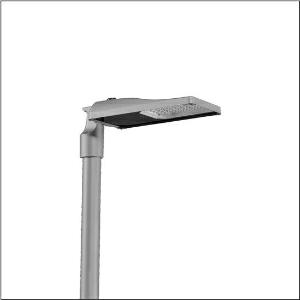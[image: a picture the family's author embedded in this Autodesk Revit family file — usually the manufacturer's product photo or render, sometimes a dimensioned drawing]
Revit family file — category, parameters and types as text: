
# Revit family: streetlight_sl_31_mini___st1_0a_5xh2d3as08ga_13ac
name_source: partatom
category: Lighting Fixtures
units: mm (PartAtom-declared; Revit-internal decimal feet)

## family parameters
Cut with Voids When Loaded = No
Host = Face
Light Source = No
Part Type = Normal
Room Calculation Point = No
Round Connector Dimension = Use Diameter
Shared = No

## types (1)
- --- (1 x LED, 5880 lm, 39.3 W, 3000K)
    Apparent Load = 39 VA
    CIE Flux Codes = 37 72 97 100 100
    Color Rendering = 70
    Color Temperature = 3000K
    Default Elevation = 1800 mm
    Description = Streetlight SL 31 mini, mast luminaire, primary light control with lens, of PMMA, primary optical cover: cover, of toughened safety glass, transparent, light distribution: ST1.0a, light emission: direct distribution, primary light characteristic: asymmetric, installation type: post-top, side-entry, LED, High Power LED, rated luminous flux: 5.880lm, luminous efficacy: 150lm/W, light colour: 730, colour temperature: 3000K, control: presetting dimming logarithmic, flexible luminous flux parameterisation, time-dependent luminous flux control, constant luminous flux control, power reduction, intelligent temperature release in ECG and LED module, overheat protection, with cable H07RN-F 2x 1.5mm², mains connection: 220..240V, AC, 50/60Hz, connection cable pre-assembled, cable length: 8,5m, start of lifetime: 39W, end of service life: 41W, reduction: 18W, luminaire housing, of diecast aluminium, powder-coated, Siteco® metallic grey (DB 702S), corrosivity category C5 high according to DIN EN ISO 12944, no sealing on luminaire upper side, inclination: -15°..+20° (post-top) | -20°..+20° (side-entry), adjustable in 5° steps, mast flange (76/60mm) included as standard, multi-level sealing system, sealing non-destructively replaceable, Smart Interface above, protection rating (complete): IP66, insulation class (complete): insulation class II (safety insulation), certification: CE, ENEC, ENEC+, VDE, UKCA, ZD4i, impact resistance: IK09, permissible operating ambient temperature for outdoor applications: -40..+50°C, standard-compliant lighting for roads and squares, packaging unit: 1 piece

Light Distribution: ST1.0a
    Height = 76 mm
    Lamp = 1 x LED
    Lamp Light Flux = 5880 lm
    Lamp Power = 39.3 W
    Lamp count = 1
    Length = 547 mm
    Luminous efficacy = 150 lm/W
    Manufacturer = Siteco
    ModVariant = No
    Model = 5XH2D3AS08GA
    Number of Poles = 1
    OnlyDefault = Yes
    Power Factor = 1
    Product Name = Streetlight SL 31 mini | ST1.0a
    Product group = mast luminaire | pylon top
    ProductGroupID = 6100
    Protection Class = Protection class II
    Protection Degree = IP 66
    RLX_Detail_Level = 1
    RLX_Emergency_Light_Flux = 0 lm
    RLX_Emergency_Type = 0
    RLX_Emergency_Type_DB = No
    RlxData = <blob elided: 39997 chars, md5=11704543>
    Socket = socket
    Standby Power = 0 W
    System Light Flux = 5880 lm
    System Power = 39 W
    Type Comments = factory setting: luminous flux: 100 % | dim-lin: 254 | 798 mA
    Type Image = l_1300330.jpg
    URL = http://relux.com
    VarID = @adj_013039
    Voltage = 0 V
    Weight = 0.00 kg
    Width = 265 mm

## geometry (parser evidence)
native form markers: Blend x4, Sweep x10
no freeform markers — native parametric forms only
